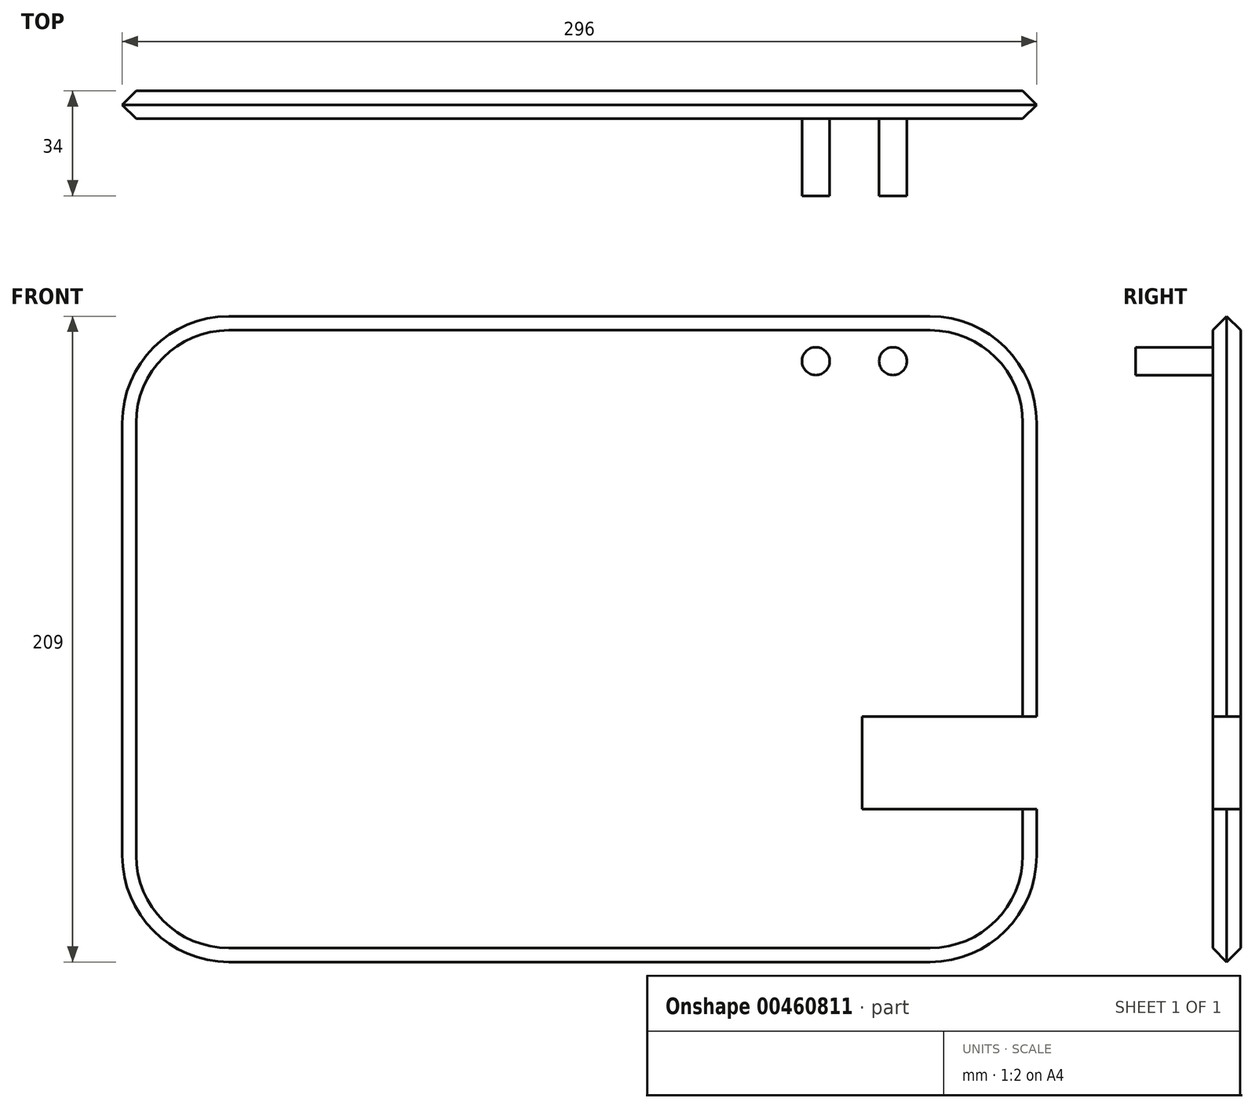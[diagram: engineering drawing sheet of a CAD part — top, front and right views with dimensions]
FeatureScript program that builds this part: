
annotation { "Feature Type Name" : "Feature", "Feature Type Description" : "" }
export const myFeature = defineFeature(function(context is Context, id is Id, definition is map)
    precondition{}
    {
        {
            var Q0;
            Q0=qCreatedBy(makeId("Front.planeOp"),FACE);
            var sketch = newSketch(context, id + "F0", { "sketchPlane" : qUnion([Q0])});
            skLineSegment(sketch, "E0.bottom", {"start": v(-113.26, 84.6) * mm, "end": v(113.74, 84.6) * mm});
            skLineSegment(sketch, "E0.top", {"start": v(-113.26, -125.4) * mm, "end": v(113.74, -125.4) * mm});
            skLineSegment(sketch, "E0.left", {"start": v(-148.26, 49.6) * mm, "end": v(-148.26, -90.4) * mm});
            skLineSegment(sketch, "E0.right", {"start": v(148.74, 49.6) * mm, "end": v(148.74, -90.4) * mm});
            skPoint(sketch, "E1.visualSharp", {"position": v(-148.26, 84.6) * mm});
            skArc(sketch, "E1.filletArc", {"start": v(-113.26, 84.6) * mm, "mid": v(-138, 74.34) * mm, "end": v(-148.26, 49.6) * mm});
            skPoint(sketch, "E2.visualSharp", {"position": v(148.74, 84.6) * mm});
            skArc(sketch, "E2.filletArc", {"start": v(148.74, 49.6) * mm, "mid": v(138.49, 74.34) * mm, "end": v(113.74, 84.6) * mm});
            skPoint(sketch, "E3.visualSharp", {"position": v(-148.26, -125.4) * mm});
            skArc(sketch, "E3.filletArc", {"start": v(-148.26, -90.4) * mm, "mid": v(-138, -115.15) * mm, "end": v(-113.26, -125.4) * mm});
            skPoint(sketch, "E4.visualSharp", {"position": v(148.74, -125.4) * mm});
            skArc(sketch, "E4.filletArc", {"start": v(113.74, -125.4) * mm, "mid": v(138.49, -115.15) * mm, "end": v(148.74, -90.4) * mm});
            skSolve(sketch);
        }
        {
            var Q0;
            Q0=makeQuery(id+"F0.imprint","IMPRINT",FACE,{"disambiguationData":[TD([[makeQuery(id+"F0.imprint","IMPRINT",EDGE,{"derivedFrom":sQuery(id+"F0.wireOp",EDGE,"E0.bottom")}),-1.0]])]});
            extrude(context, id + "F1", {"entities" : qUnion([Q0]), "depth" : 9 * mm});
        }
        {
            var Q0;
            Q0=makeQuery(id+"F1.opExtrude","CAP_FACE",FACE,{"disambiguationData":[OSD([sQuery(id+"F0.wireOp",EDGE,"E0.bottom"),sQuery(id+"F0.wireOp",EDGE,"E0.top"),sQuery(id+"F0.wireOp",EDGE,"E0.left"),sQuery(id+"F0.wireOp",EDGE,"E0.right"),sQuery(id+"F0.wireOp",EDGE,"E1.filletArc"),sQuery(id+"F0.wireOp",EDGE,"E2.filletArc"),sQuery(id+"F0.wireOp",EDGE,"E3.filletArc"),sQuery(id+"F0.wireOp",EDGE,"E4.filletArc")])],"isStart":false});
            var sketch = newSketch(context, id + "F2", { "sketchPlane" : qUnion([Q0])});
            skCircle(sketch, "E5", {"center": v(101.74, 69.6) * mm, "radius": 4.5 * mm});
            skCircle(sketch, "E6", {"center": v(76.74, 69.6) * mm, "radius": 4.5 * mm});
            skSolve(sketch);
        }
        {
            var Q0;
            Q0=makeQuery(id+"F2.imprint","IMPRINT",FACE,{"disambiguationData":[TD([[makeQuery(id+"F2.imprint","IMPRINT",EDGE,{"derivedFrom":sQuery(id+"F2.wireOp",EDGE,"E5")}),1.0]])]});
            var Q1;
            Q1=makeQuery(id+"F2.imprint","IMPRINT",FACE,{"disambiguationData":[TD([[makeQuery(id+"F2.imprint","IMPRINT",EDGE,{"derivedFrom":sQuery(id+"F2.wireOp",EDGE,"E6")}),1.0]])]});
            extrude(context, id + "F3", {"entities" : qUnion([Q0, Q1]), "operationType" : NewBodyOperationType.ADD, "depth" : 25 * mm});
        }
        {
            var Q0;
            Q0=makeQuery(id+"F1.opExtrude","CAP_FACE",FACE,{"disambiguationData":[OSD([sQuery(id+"F0.wireOp",EDGE,"E0.bottom"),sQuery(id+"F0.wireOp",EDGE,"E0.top"),sQuery(id+"F0.wireOp",EDGE,"E0.left"),sQuery(id+"F0.wireOp",EDGE,"E0.right"),sQuery(id+"F0.wireOp",EDGE,"E1.filletArc"),sQuery(id+"F0.wireOp",EDGE,"E2.filletArc"),sQuery(id+"F0.wireOp",EDGE,"E3.filletArc"),sQuery(id+"F0.wireOp",EDGE,"E4.filletArc")])],"isStart":false});
            var sketch = newSketch(context, id + "F4", { "sketchPlane" : qUnion([Q0])});
            skLineSegment(sketch, "E7.bottom", {"start": v(91.74, -45.4) * mm, "end": v(180.59, -45.4) * mm});
            skLineSegment(sketch, "E7.top", {"start": v(91.74, -75.4) * mm, "end": v(180.59, -75.4) * mm});
            skLineSegment(sketch, "E7.left", {"start": v(91.74, -45.4) * mm, "end": v(91.74, -75.4) * mm});
            skLineSegment(sketch, "E7.right", {"start": v(180.59, -45.4) * mm, "end": v(180.59, -75.4) * mm});
            skSolve(sketch);
        }
        {
            var Q0;
            {var subQ0=sQuery(id+"F4.wireOp",EDGE,"E7.left");Q0=makeQuery(id+"F4.imprint","IMPRINT",FACE,{"disambiguationData":[TD([[makeQuery(id+"F4.imprint","IMPRINT",EDGE,{"derivedFrom":subQ0}),1.0]])]});}
            extrude(context, id + "F5", {"entities" : qUnion([Q0]), "operationType" : NewBodyOperationType.REMOVE, "oppositeDirection" : true, "depth" : 25 * mm});
        }
        {
            var Q0;
            Q0=makeQuery(id+"F1.opExtrude","CAP_EDGE",EDGE,{"disambiguationData":[OSD([sQuery(id+"F0.wireOp",EDGE,"E0.bottom")])],"isStart":false});
            chamfer(context, id + "F6", {"entities" : qUnion([Q0]), "width" : 5 * mm, "tangentPropagation" : true});
        }
        {
            var Q0;
            Q0=makeQuery(id+"F1.opExtrude","CAP_EDGE",EDGE,{"disambiguationData":[OSD([sQuery(id+"F0.wireOp",EDGE,"E2.filletArc")])],"isStart":true});
            chamfer(context, id + "F7", {"entities" : qUnion([Q0]), "width" : 5 * mm, "tangentPropagation" : true});
        }
    });
